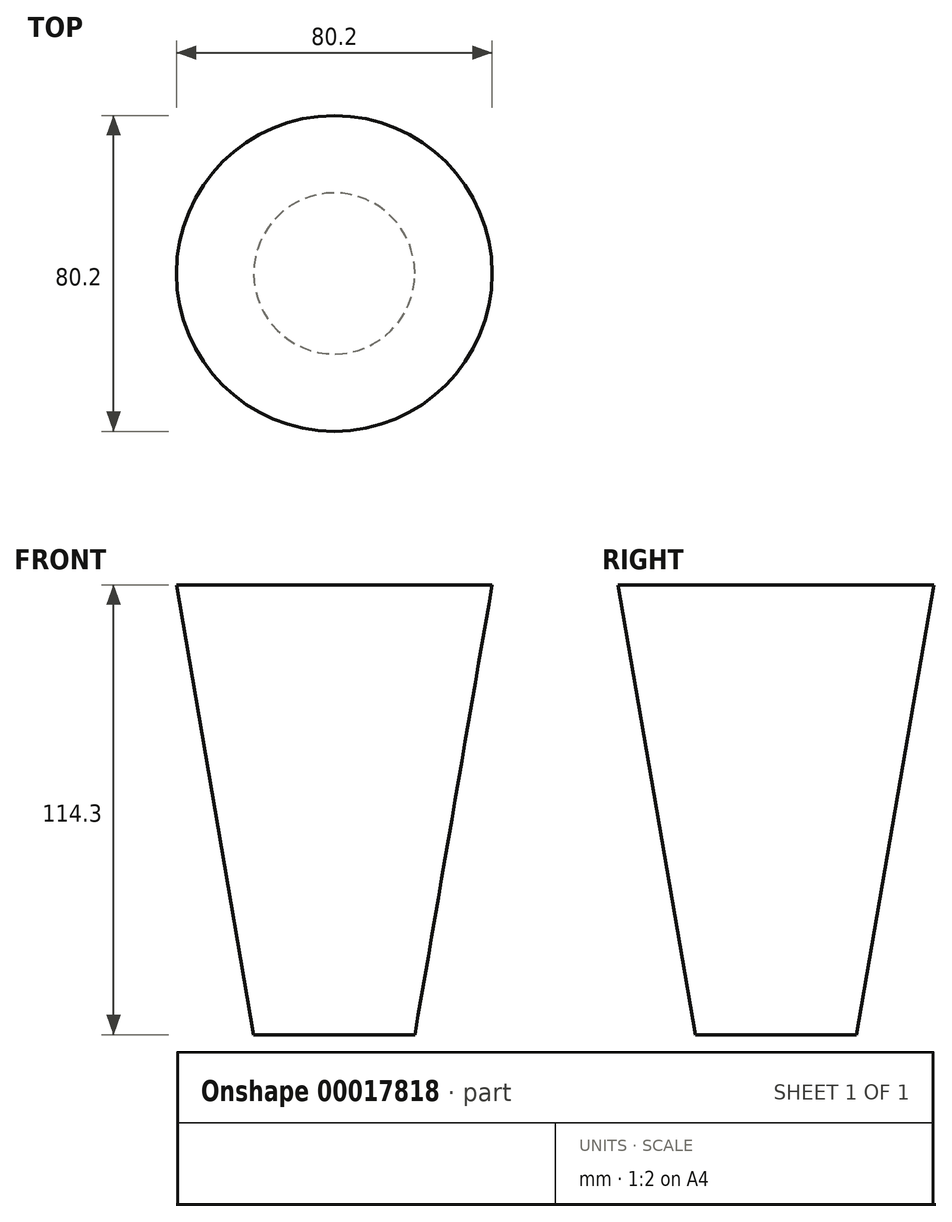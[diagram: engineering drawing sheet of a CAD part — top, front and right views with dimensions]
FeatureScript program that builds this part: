
annotation { "Feature Type Name" : "Feature", "Feature Type Description" : "" }
export const myFeature = defineFeature(function(context is Context, id is Id, definition is map)
    precondition{}
    {
        {
            var Q0;
            Q0=qCreatedBy(makeId("Top.planeOp"),FACE);
            cPlane(context, id + "F0", {"entities" : qUnion([Q0]), "cplaneType" : CPlaneType.OFFSET, "offset" : 114.3 * mm, "width" : 152.4 * mm, "height" : 152.4 * mm});
        }
        {
            var Q0;
            Q0=qCreatedBy(makeId("Top.planeOp"),FACE);
            var sketch = newSketch(context, id + "F1", { "sketchPlane" : qUnion([Q0])});
            skCircle(sketch, "E0", {"center": v(0, 0) * mm, "radius": 20.46 * mm});
            skSolve(sketch);
        }
        {
            var Q0;
            Q0=qCreatedBy(id+"F0.planeOp",FACE);
            var sketch = newSketch(context, id + "F2", { "sketchPlane" : qUnion([Q0])});
            skCircle(sketch, "E1", {"center": v(0, 0) * mm, "radius": 40.1 * mm});
            skSolve(sketch);
        }
        {
            var Q0;
            Q0=makeQuery(id+"F2.imprint","IMPRINT",FACE,{"disambiguationData":[TD([[makeQuery(id+"F2.imprint","IMPRINT",EDGE,{"derivedFrom":sQuery(id+"F2.wireOp",EDGE,"E1")}),1.0]])]});
            var Q1;
            Q1=makeQuery(id+"F1.imprint","IMPRINT",FACE,{"disambiguationData":[TD([[makeQuery(id+"F1.imprint","IMPRINT",EDGE,{"derivedFrom":sQuery(id+"F1.wireOp",EDGE,"E0")}),1.0]])]});
            loft(context, id + "F3", {"sheetProfilesArray" : [{ "sheetProfileEntities" : qUnion([Q0]) }, { "sheetProfileEntities" : qUnion([Q1]) }]});
        }
    });
